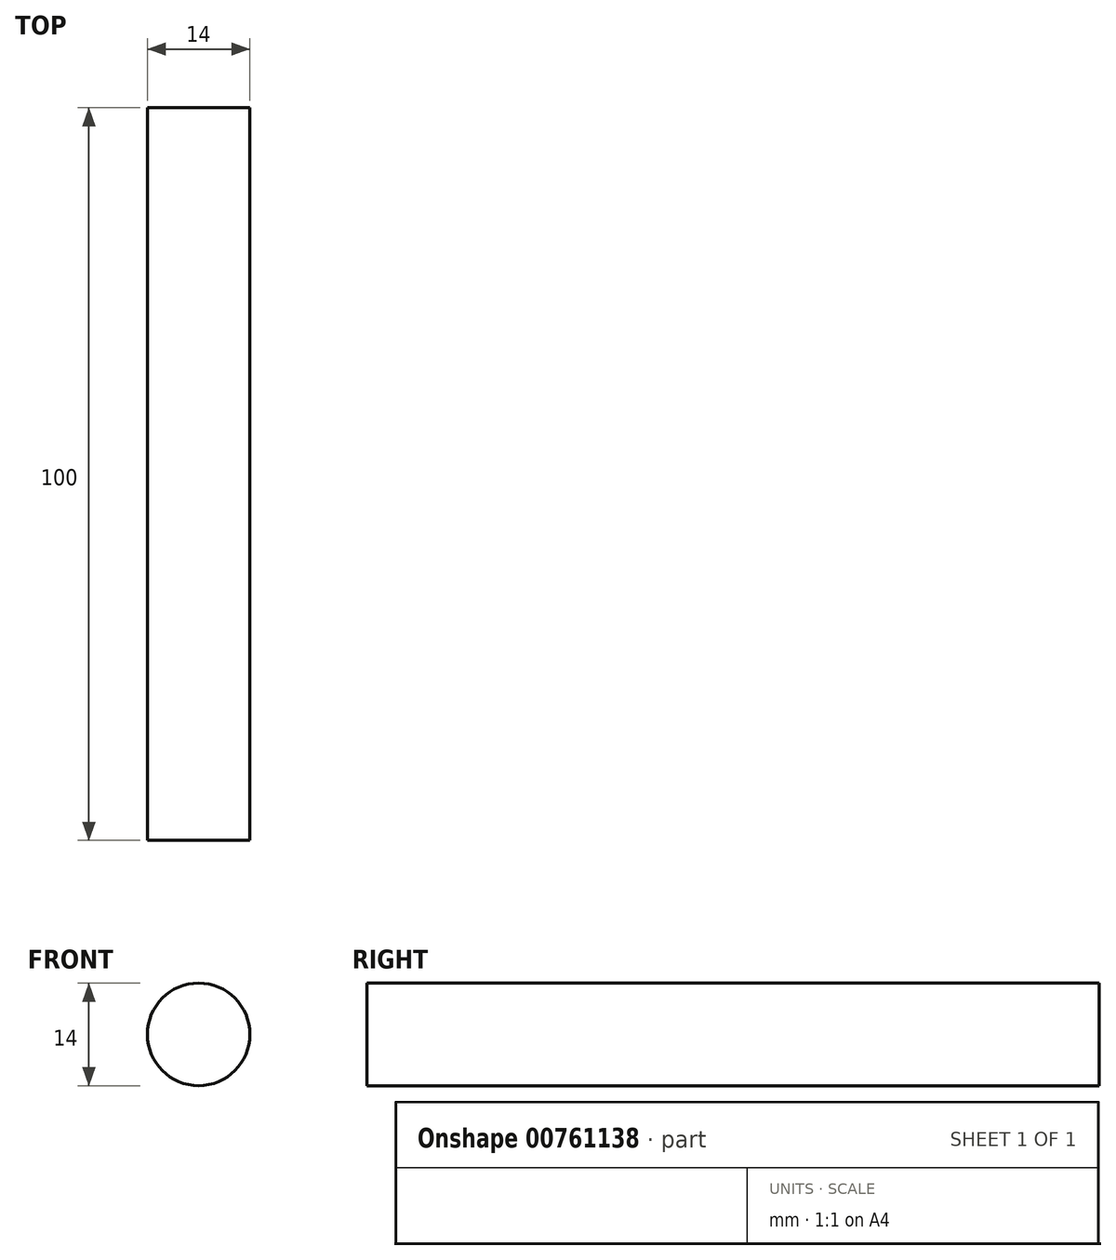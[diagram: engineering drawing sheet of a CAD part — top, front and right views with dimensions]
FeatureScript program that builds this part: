
annotation { "Feature Type Name" : "Feature", "Feature Type Description" : "" }
export const myFeature = defineFeature(function(context is Context, id is Id, definition is map)
    precondition{}
    {
        {
            var Q0;
            Q0=qCreatedBy(makeId("Front.planeOp"),FACE);
            var sketch = newSketch(context, id + "F0", { "sketchPlane" : qUnion([Q0])});
            skCircle(sketch, "E0", {"center": v(0, 0) * mm, "radius": 7 * mm});
            skSolve(sketch);
        }
        {
            var Q0;
            Q0=makeQuery(id+"F0.imprint","IMPRINT",FACE,{"disambiguationData":[TD([[makeQuery(id+"F0.imprint","IMPRINT",EDGE,{"derivedFrom":sQuery(id+"F0.wireOp",EDGE,"E0")}),1.0]])]});
            extrude(context, id + "F1", {"entities" : qUnion([Q0]), "depth" : 100 * mm, "offsetDistance" : 25 * mm});
        }
    });
